# Revit family: Flachverbinder 40-5 4-Loch
name_source: partatom
category: HLS-Bauteile
revit_build: Autodesk Revit 2017 (Build: 20190507_1515(x64)
units: mm (PartAtom-declared; Revit-internal decimal feet)

## family parameters
Arbeitsebenenbasiert = Ja
Beim Laden mit Abzugskörper schneiden = Nein
Bemaßung runder Anschluss = Durchmesser verwenden
Gemeinsam genutzt = Ja
Immer vertikal = Nein
Raumberechnungspunkt = Nein
Teiletyp = Normal

## types (1)
- Flachverbinder 40-5 4-Loch
    Artikelnummer = 0814349
    B = 40 mm  [stored 0.131234 ft]
    Breite = 40 mm  [stored 0.131234 ft]
    EAN = 4250928419972
    Fabrikat = MEFA
    Firma = MEFA Befestigungs- und Montagesysteme GmbH
    Gewicht = 0.25 kg
    Gewicht pro Bauteil = 0.25 kg
    Kurztext1 = Flachverbinder 4-Lo.
    Kurztext2 = für C-Profil 45 Lochung 13 mm
    L = 176 mm  [stored 0.577428 ft]
    Lochdurchmesser = 13 mm
    Länge = 176 mm  [stored 0.577428 ft]
    Material = Stahl
    Materialname = S235
    Mengeneinheit = St
    Oberflaeche = galvanisch verzinkt
    Profil = C-Profil
    Profiltyp = 45
    S = 5 mm  [stored 0.0164042 ft]
    Sicherheitsfaktor = 0
    Stärke = 5 mm  [stored 0.0164042 ft]
    Vorgabe-Ansicht = 1219 mm
    max. zul. Last Fx = 0.00 kN
    max. zul. Last Fx XL100+120 = 0.00 kN
    max. zul. Last Fz = 0.00 kN
    max. zul. Last Fz XL100+120 = 0.00 kN
    max. zul. Moment XL100+120 = 0.00 kN-m
    vpe = 25 St

note: [stored X ft] marks values corroborated as IEEE doubles in the binary element streams (Revit-internal decimal feet)
